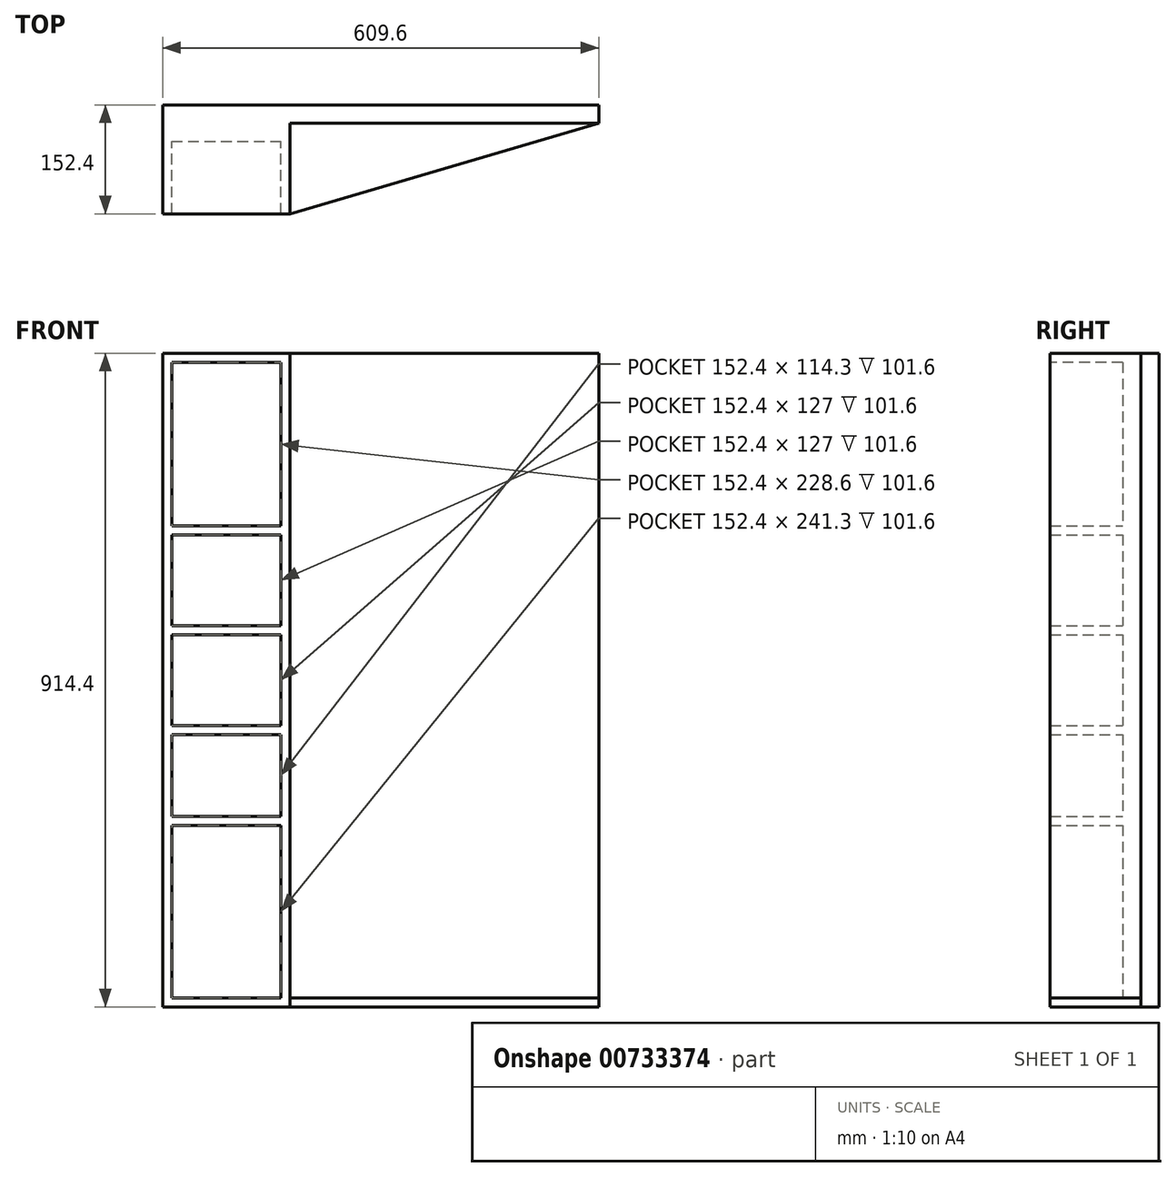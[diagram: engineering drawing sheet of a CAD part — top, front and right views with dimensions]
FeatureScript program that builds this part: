
annotation { "Feature Type Name" : "Feature", "Feature Type Description" : "" }
export const myFeature = defineFeature(function(context is Context, id is Id, definition is map)
    precondition{}
    {
        {
            var Q0;
            Q0=qCreatedBy(makeId("Front.planeOp"),FACE);
            var sketch = newSketch(context, id + "F0", { "sketchPlane" : qUnion([Q0])});
            skLineSegment(sketch, "E0.bottom", {"start": v(0, 0) * mm, "end": v(609.6, 0) * mm});
            skLineSegment(sketch, "E0.top", {"start": v(0, 914.4) * mm, "end": v(609.6, 914.4) * mm});
            skLineSegment(sketch, "E0.left", {"start": v(0, 0) * mm, "end": v(0, 914.4) * mm});
            skLineSegment(sketch, "E0.right", {"start": v(609.6, 0) * mm, "end": v(609.6, 914.4) * mm});
            skSolve(sketch);
        }
        {
            var Q0;
            Q0=makeQuery(id+"F0.imprint","IMPRINT",FACE,{"disambiguationData":[TD([[makeQuery(id+"F0.imprint","IMPRINT",EDGE,{"derivedFrom":sQuery(id+"F0.wireOp",EDGE,"E0.bottom")}),1.0]])]});
            extrude(context, id + "F1", {"entities" : qUnion([Q0]), "depth" : 25.4 * mm, "offsetDistance" : 25.4 * mm});
        }
        {
            var Q0;
            Q0=makeQuery(id+"F1.opExtrude","CAP_FACE",FACE,{"disambiguationData":[OSD([sQuery(id+"F0.wireOp",EDGE,"E0.bottom"),sQuery(id+"F0.wireOp",EDGE,"E0.top"),sQuery(id+"F0.wireOp",EDGE,"E0.left"),sQuery(id+"F0.wireOp",EDGE,"E0.right")])],"isStart":false});
            var sketch = newSketch(context, id + "F2", { "sketchPlane" : qUnion([Q0])});
            skLineSegment(sketch, "E1.bottom", {"start": v(0, 0) * mm, "end": v(177.8, 0) * mm});
            skLineSegment(sketch, "E1.top", {"start": v(0, 914.4) * mm, "end": v(177.8, 914.4) * mm});
            skLineSegment(sketch, "E1.left", {"start": v(0, 0) * mm, "end": v(0, 914.4) * mm});
            skLineSegment(sketch, "E1.right", {"start": v(177.8, 0) * mm, "end": v(177.8, 914.4) * mm});
            skSolve(sketch);
        }
        {
            var Q0;
            Q0=makeQuery(id+"F2.imprint","IMPRINT",FACE,{"disambiguationData":[TD([[makeQuery(id+"F2.imprint","IMPRINT",EDGE,{"derivedFrom":sQuery(id+"F2.wireOp",EDGE,"E1.bottom")}),1.0]])]});
            extrude(context, id + "F3", {"entities" : qUnion([Q0]), "operationType" : NewBodyOperationType.ADD, "depth" : 127 * mm, "offsetDistance" : 25.4 * mm});
        }
        {
            var Q0;
            Q0=makeQuery(id+"F3.opExtrude","CAP_FACE",FACE,{"disambiguationData":[OSD([sQuery(id+"F2.wireOp",EDGE,"E1.bottom"),sQuery(id+"F2.wireOp",EDGE,"E1.top"),sQuery(id+"F2.wireOp",EDGE,"E1.left"),sQuery(id+"F2.wireOp",EDGE,"E1.right")])],"isStart":false});
            var sketch = newSketch(context, id + "F4", { "sketchPlane" : qUnion([Q0])});
            skLineSegment(sketch, "E2.bottom", {"start": v(12.7, 901.7) * mm, "end": v(165.1, 901.7) * mm});
            skLineSegment(sketch, "E2.top", {"start": v(12.7, 12.7) * mm, "end": v(165.1, 12.7) * mm});
            skLineSegment(sketch, "E2.left", {"start": v(12.7, 901.7) * mm, "end": v(12.7, 12.7) * mm});
            skLineSegment(sketch, "E2.right", {"start": v(165.1, 901.7) * mm, "end": v(165.1, 12.7) * mm});
            skSolve(sketch);
        }
        {
            var Q0;
            Q0=makeQuery(id+"F4.imprint","IMPRINT",FACE,{"disambiguationData":[TD([[makeQuery(id+"F4.imprint","IMPRINT",EDGE,{"derivedFrom":sQuery(id+"F4.wireOp",EDGE,"E2.bottom")}),-1.0]])]});
            extrude(context, id + "F5", {"entities" : qUnion([Q0]), "operationType" : NewBodyOperationType.REMOVE, "oppositeDirection" : true, "depth" : 101.6 * mm, "offsetDistance" : 25.4 * mm});
        }
        {
            var Q0;
            Q0=makeQuery(id+"F5.boolean.opBoolean","COPY",FACE,{"derivedFrom":makeQuery(id+"F5.opExtrude","CAP_FACE",FACE,{"disambiguationData":[OSD([sQuery(id+"F4.wireOp",EDGE,"E2.bottom"),sQuery(id+"F4.wireOp",EDGE,"E2.top"),sQuery(id+"F4.wireOp",EDGE,"E2.left"),sQuery(id+"F4.wireOp",EDGE,"E2.right")])],"isStart":false})});
            var sketch = newSketch(context, id + "F6", { "sketchPlane" : qUnion([Q0])});
            skLineSegment(sketch, "E3.bottom", {"start": v(12.7, 673.1) * mm, "end": v(165.1, 673.1) * mm});
            skLineSegment(sketch, "E3.top", {"start": v(12.7, 660.4) * mm, "end": v(165.1, 660.4) * mm});
            skLineSegment(sketch, "E3.left", {"start": v(12.7, 673.1) * mm, "end": v(12.7, 660.4) * mm});
            skLineSegment(sketch, "E3.right", {"start": v(165.1, 673.1) * mm, "end": v(165.1, 660.4) * mm});
            skLineSegment(sketch, "E4.bottom", {"start": v(12.7, 533.4) * mm, "end": v(165.1, 533.4) * mm});
            skLineSegment(sketch, "E4.top", {"start": v(12.7, 520.7) * mm, "end": v(165.1, 520.7) * mm});
            skLineSegment(sketch, "E4.left", {"start": v(12.7, 533.4) * mm, "end": v(12.7, 520.7) * mm});
            skLineSegment(sketch, "E4.right", {"start": v(165.1, 533.4) * mm, "end": v(165.1, 520.7) * mm});
            skLineSegment(sketch, "E5.bottom", {"start": v(12.7, 381) * mm, "end": v(165.1, 381) * mm});
            skLineSegment(sketch, "E5.top", {"start": v(12.7, 393.7) * mm, "end": v(165.1, 393.7) * mm});
            skLineSegment(sketch, "E5.left", {"start": v(12.7, 381) * mm, "end": v(12.7, 393.7) * mm});
            skLineSegment(sketch, "E5.right", {"start": v(165.1, 381) * mm, "end": v(165.1, 393.7) * mm});
            skLineSegment(sketch, "E6.bottom", {"start": v(12.7, 254) * mm, "end": v(165.1, 254) * mm});
            skLineSegment(sketch, "E6.top", {"start": v(12.7, 266.7) * mm, "end": v(165.1, 266.7) * mm});
            skLineSegment(sketch, "E6.left", {"start": v(12.7, 254) * mm, "end": v(12.7, 266.7) * mm});
            skLineSegment(sketch, "E6.right", {"start": v(165.1, 254) * mm, "end": v(165.1, 266.7) * mm});
            skSolve(sketch);
        }
        {
            var Q0;
            Q0=makeQuery(id+"F6.imprint","IMPRINT",FACE,{"disambiguationData":[TD([[makeQuery(id+"F6.imprint","IMPRINT",EDGE,{"derivedFrom":sQuery(id+"F6.wireOp",EDGE,"E3.bottom")}),-1.0]])]});
            var Q1;
            Q1=makeQuery(id+"F6.imprint","IMPRINT",FACE,{"disambiguationData":[TD([[makeQuery(id+"F6.imprint","IMPRINT",EDGE,{"derivedFrom":sQuery(id+"F6.wireOp",EDGE,"E4.bottom")}),-1.0]])]});
            var Q2;
            Q2=makeQuery(id+"F6.imprint","IMPRINT",FACE,{"disambiguationData":[TD([[makeQuery(id+"F6.imprint","IMPRINT",EDGE,{"derivedFrom":sQuery(id+"F6.wireOp",EDGE,"E5.bottom")}),1.0]])]});
            var Q3;
            Q3=makeQuery(id+"F6.imprint","IMPRINT",FACE,{"disambiguationData":[TD([[makeQuery(id+"F6.imprint","IMPRINT",EDGE,{"derivedFrom":sQuery(id+"F6.wireOp",EDGE,"E6.bottom")}),1.0]])]});
            extrude(context, id + "F7", {"entities" : qUnion([Q0, Q1, Q2, Q3]), "operationType" : NewBodyOperationType.ADD, "depth" : 101.6 * mm, "offsetDistance" : 25.4 * mm});
        }
        {
            var Q0;
            Q0=qCreatedBy(makeId("Top.planeOp"),FACE);
            var sketch = newSketch(context, id + "F8", { "sketchPlane" : qUnion([Q0])});
            skLineSegment(sketch, "E7", {"start": v(177.8, -152.4) * mm, "end": v(609.6, -25.4) * mm});
            skLineSegment(sketch, "E8", {"start": v(177.8, -25.4) * mm, "end": v(609.6, -25.4) * mm});
            skLineSegment(sketch, "E9", {"start": v(177.8, -25.4) * mm, "end": v(177.8, -152.4) * mm});
            skSolve(sketch);
        }
        {
            var Q0;
            Q0=makeQuery(id+"F8.imprint","IMPRINT",FACE,{"disambiguationData":[TD([[makeQuery(id+"F8.imprint","IMPRINT",EDGE,{"derivedFrom":sQuery(id+"F8.wireOp",EDGE,"E7")}),1.0]])]});
            extrude(context, id + "F9", {"entities" : qUnion([Q0]), "operationType" : NewBodyOperationType.ADD, "depth" : 12.7 * mm, "offsetDistance" : 25.4 * mm});
        }
    });
